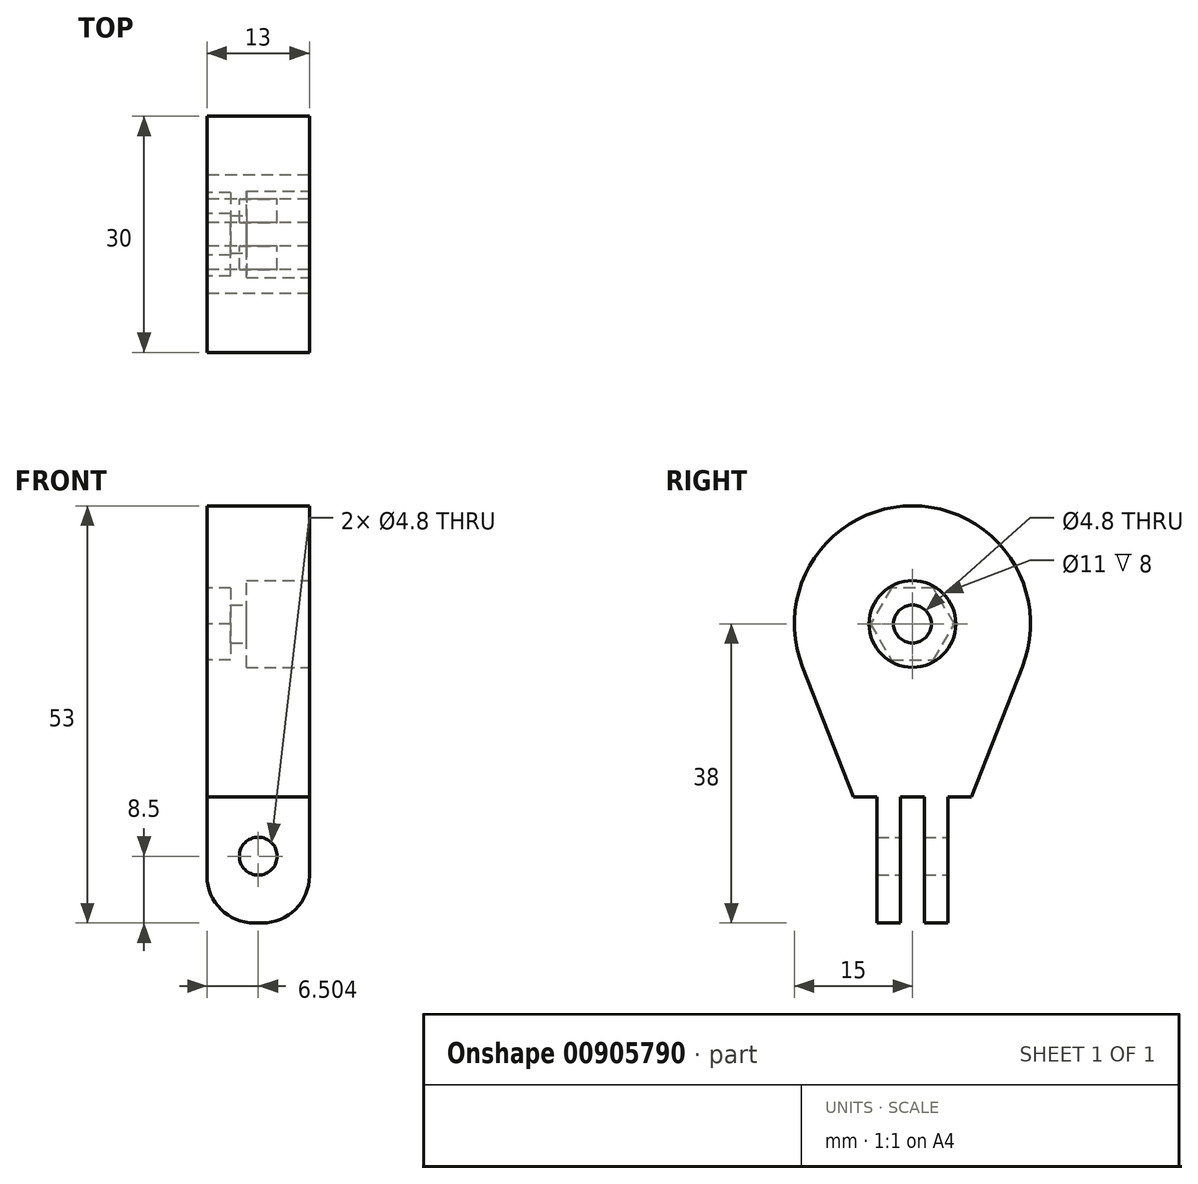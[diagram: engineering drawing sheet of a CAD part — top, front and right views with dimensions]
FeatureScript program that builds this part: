
annotation { "Feature Type Name" : "Feature", "Feature Type Description" : "" }
export const myFeature = defineFeature(function(context is Context, id is Id, definition is map)
    precondition{}
    {
        {
            var Q0;
            Q0=qCreatedBy(makeId("Top.planeOp"),FACE);
            var sketch = newSketch(context, id + "F0", { "sketchPlane" : qUnion([Q0])});
            skLineSegment(sketch, "E0.right", {"start": v(52.22, -25.13) * mm, "end": v(52.22, -14.87) * mm});
            skPoint(sketch, "E0.middle", {"position": v(48.22, 0) * mm});
            skLineSegment(sketch, "E1.bottom", {"start": v(52.22, 30) * mm, "end": v(43.22, 30) * mm});
            skLineSegment(sketch, "E1.top", {"start": v(52.22, -30) * mm, "end": v(43.22, -30) * mm});
            skLineSegment(sketch, "E1.left", {"start": v(52.22, 30) * mm, "end": v(52.22, -30) * mm});
            skLineSegment(sketch, "E1.right", {"start": v(43.22, 30) * mm, "end": v(43.22, -30) * mm});
            skPoint(sketch, "E2.visualSharp", {"position": v(43.22, 30) * mm});
            skLineSegment(sketch, "E2.filletArc", {"start": v(43.22, 30) * mm, "end": v(43.22, 30) * mm});
            skPoint(sketch, "E3.visualSharp", {"position": v(43.22, -30) * mm});
            skLineSegment(sketch, "E3.filletArc", {"start": v(43.22, -30) * mm, "end": v(43.22, -30) * mm});
            skPoint(sketch, "E4.visualSharp", {"position": v(52.22, 30) * mm});
            skLineSegment(sketch, "E4.filletArc", {"start": v(52.22, 30) * mm, "end": v(52.22, 30) * mm});
            skPoint(sketch, "E5.visualSharp", {"position": v(52.22, -30) * mm});
            skLineSegment(sketch, "E5.filletArc", {"start": v(52.22, -30) * mm, "end": v(52.22, -30) * mm});
            skSolve(sketch);
        }
        {
            var Q0;
            Q0=makeQuery(id+"F0.imprint","IMPRINT",FACE,{"disambiguationData":[TD([[makeQuery(id+"F0.imprint","IMPRINT",EDGE,{"derivedFrom":sQuery(id+"F0.wireOp",EDGE,"E1.bottom")}),1.0]])]});
            extrude(context, id + "F1", {"entities" : qUnion([Q0]), "depth" : 30 * mm, "offsetDistance" : 25 * mm, "hasSecondDirection" : true, "secondDirectionOppositeDirection" : true, "secondDirectionDepth" : 22 * mm});
        }
        {
            var Q0;
            Q0=makeQuery(id+"F1.opExtrude","SWEPT_FACE",FACE,{"disambiguationData":[OSD([sQuery(id+"F0.wireOp",EDGE,"E1.left")])]});
            var sketch = newSketch(context, id + "F2", { "sketchPlane" : qUnion([Q0])});
            skCircle(sketch, "E6", {"center": v(0, 0) * mm, "radius": 5.5 * mm});
            skCircle(sketch, "E7", {"center": v(0, 0) * mm, "radius": 2.4 * mm});
            skSolve(sketch);
        }
        {
            var Q0;
            Q0=makeQuery(id+"F2.imprint","IMPRINT",FACE,{"disambiguationData":[TD([[makeQuery(id+"F2.imprint","IMPRINT",EDGE,{"derivedFrom":sQuery(id+"F2.wireOp",EDGE,"E7")}),-1.0]])]});
            var Q1;
            {var subQ0=sQuery(id+"F2.wireOp",EDGE,"E6");var subQ1=sQuery(id+"F0.wireOp",EDGE,"E1.left");var subQ2=makeQuery(id+"Ft0UKXCdEgkPogb_1.opFillet","BLEND_EDGE",EDGE,{"blendedFrom":[makeQuery(id+"F1.opExtrude","CAP_EDGE",EDGE,{"disambiguationData":[OSD([subQ1])],"isStart":false}),makeQuery(id+"F1.opExtrude","SWEPT_FACE",FACE,{"disambiguationData":[OSD([subQ1])]})],"blendedInto":[makeQuery(id+"F1.opExtrude","SWEPT_FACE",FACE,{"disambiguationData":[OSD([subQ1])]})]});var subQ3=makeQuery(id+"F2.imprint","INTERSECT",VERTEX,{"disambiguationData":[OD(0.0)],"derivedFrom":[subQ2,subQ0]});Q1=makeQuery(id+"F2.imprint","IMPRINT",FACE,{"disambiguationData":[TD([[makeQuery(id+"F2.imprint","IMPRINT",EDGE,{"disambiguationData":[TD([[subQ3,-1.0]])],"derivedFrom":subQ0}),1.0]])]});}
            extrude(context, id + "F3", {"entities" : qUnion([Q0, Q1]), "operationType" : NewBodyOperationType.REMOVE, "oppositeDirection" : true, "depth" : 4 * mm, "offsetDistance" : 25 * mm});
        }
        {
            var Q0;
            Q0=makeQuery(id+"F3.boolean.opBoolean","SPLIT",FACE,{"disambiguationData":[TD([makeQuery(id+"F3.opExtrude","SWEPT_FACE",FACE,{"disambiguationData":[OSD([sQuery(id+"F2.wireOp",EDGE,"E7")])]})])],"derivedFrom":makeQuery(id+"F1.opExtrude","SWEPT_FACE",FACE,{"disambiguationData":[OSD([sQuery(id+"F0.wireOp",EDGE,"E1.left")])]})});
            extrude(context, id + "F4", {"entities" : qUnion([Q0]), "operationType" : NewBodyOperationType.REMOVE, "oppositeDirection" : true, "depth" : 10.6 * mm, "offsetDistance" : 25 * mm});
        }
        {
            var Q0;
            Q0=makeQuery(id+"F1.opExtrude","SWEPT_FACE",FACE,{"disambiguationData":[OSD([sQuery(id+"F0.wireOp",EDGE,"E1.right")])]});
            var sketch = newSketch(context, id + "F5", { "sketchPlane" : qUnion([Q0])});
            skCircle(sketch, "E8.cCircle", {"center": v(0, 0) * mm, "radius": 5.31 * mm, "construction": true});
            skLineSegment(sketch, "E8.0", {"start": v(5.31, 0) * mm, "end": v(2.66, -4.6) * mm});
            skLineSegment(sketch, "E8.1", {"start": v(2.66, -4.6) * mm, "end": v(-2.66, -4.6) * mm});
            skLineSegment(sketch, "E8.2", {"start": v(-2.66, -4.6) * mm, "end": v(-5.31, 0) * mm});
            skLineSegment(sketch, "E8.3", {"start": v(-5.31, 0) * mm, "end": v(-2.66, 4.6) * mm});
            skLineSegment(sketch, "E8.4", {"start": v(-2.66, 4.6) * mm, "end": v(2.66, 4.6) * mm});
            skLineSegment(sketch, "E8.5", {"start": v(2.66, 4.6) * mm, "end": v(5.31, 0) * mm});
            skSolve(sketch);
        }
        {
            var Q0;
            {var subQ8=sQuery(id+"F5.wireOp",EDGE,"E8.0");Q0=makeQuery(id+"F5.imprint","IMPRINT",FACE,{"disambiguationData":[TD([[makeQuery(id+"F5.imprint","IMPRINT",EDGE,{"derivedFrom":subQ8}),-1.0]])]});}
            var Q1;
            {var subQ0=sQuery(id+"F5.wireOp",EDGE,"E8.4");Q1=makeQuery(id+"F5.imprint","IMPRINT",FACE,{"disambiguationData":[TD([[makeQuery(id+"F5.imprint","IMPRINT",EDGE,{"derivedFrom":subQ0}),-1.0]])]});}
            extrude(context, id + "F6", {"entities" : qUnion([Q0, Q1]), "operationType" : NewBodyOperationType.REMOVE, "oppositeDirection" : true, "depth" : 3 * mm, "offsetDistance" : 25 * mm});
        }
        {
            var Q0;
            Q0=makeQuery(id+"F1.opExtrude","SWEPT_FACE",FACE,{"disambiguationData":[OSD([sQuery(id+"F0.wireOp",EDGE,"E1.right")])]});
            var sketch = newSketch(context, id + "F7", { "sketchPlane" : qUnion([Q0])});
            skArc(sketch, "E9", {"start": v(13.97, -5.47) * mm, "mid": v(0, 15) * mm, "end": v(-13.97, -5.47) * mm});
            skLineSegment(sketch, "E10", {"start": v(0, -22) * mm, "end": v(-7.5, -22) * mm});
            skLineSegment(sketch, "E11", {"start": v(-7.5, -22) * mm, "end": v(-13.97, -5.47) * mm});
            skLineSegment(sketch, "E12.MirrorCS", {"start": v(7.5, -22) * mm, "end": v(13.97, -5.47) * mm});
            skLineSegment(sketch, "E13.MirrorCS", {"start": v(0, -22) * mm, "end": v(7.5, -22) * mm});
            skSolve(sketch);
        }
        {
            var Q0;
            Q0=makeQuery(id+"F7.imprint","IMPRINT",FACE,{"disambiguationData":[TD([[makeQuery(id+"F7.imprint","IMPRINT",EDGE,{"derivedFrom":sQuery(id+"F7.wireOp",EDGE,"E9")}),-1.0]])]});
            extrude(context, id + "F8", {"entities" : qUnion([Q0]), "operationType" : NewBodyOperationType.REMOVE, "oppositeDirection" : true, "depth" : 25 * mm, "offsetDistance" : 25 * mm});
        }
        {
            var Q0;
            {var subQ2=sQuery(id+"F0.wireOp",EDGE,"E1.left");var subQ3=sQuery(id+"F0.wireOp",EDGE,"E1.bottom");Q0=makeQuery(id+"F3.boolean.opBoolean","SPLIT",FACE,{"disambiguationData":[TD([makeQuery(id+"F1.opExtrude","SWEPT_FACE",FACE,{"disambiguationData":[OSD([subQ3])]})])],"derivedFrom":makeQuery(id+"F1.opExtrude","SWEPT_FACE",FACE,{"disambiguationData":[OSD([subQ2])]})});}
            extrude(context, id + "F9", {"entities" : qUnion([Q0]), "operationType" : NewBodyOperationType.ADD, "depth" : 4 * mm, "offsetDistance" : 25 * mm});
        }
        {
            var Q0;
            {var subQ0=sQuery(id+"F0.wireOp",EDGE,"E1.left");Q0=makeQuery(id+"F9.boolean.opBoolean","MERGE",FACE,{"derivedFrom":[makeQuery(id+"F1.opExtrude","CAP_FACE",FACE,{"disambiguationData":[OSD([sQuery(id+"F0.wireOp",EDGE,"E1.bottom"),sQuery(id+"F0.wireOp",EDGE,"E1.top"),subQ0,sQuery(id+"F0.wireOp",EDGE,"E1.right")])],"isStart":true}),makeQuery(id+"F9.opExtrude","SWEPT_FACE",FACE,{"disambiguationData":[OSD([subQ0])]})]});}
            var sketch = newSketch(context, id + "F10", { "sketchPlane" : qUnion([Q0])});
            skLineSegment(sketch, "E14", {"start": v(56.22, 0) * mm, "end": v(56.22, -1.5) * mm});
            skLineSegment(sketch, "E15.bottom", {"start": v(56.22, -1.5) * mm, "end": v(43.22, -1.5) * mm});
            skLineSegment(sketch, "E15.top", {"start": v(56.22, -4.5) * mm, "end": v(43.22, -4.5) * mm});
            skLineSegment(sketch, "E15.left", {"start": v(56.22, -1.5) * mm, "end": v(56.22, -4.5) * mm});
            skLineSegment(sketch, "E15.right", {"start": v(43.22, -1.5) * mm, "end": v(43.22, -4.5) * mm});
            skLineSegment(sketch, "E16.MirrorCS", {"start": v(56.22, 1.5) * mm, "end": v(43.22, 1.5) * mm});
            skLineSegment(sketch, "E17.MirrorCS", {"start": v(56.22, 4.5) * mm, "end": v(43.22, 4.5) * mm});
            skLineSegment(sketch, "E18.MirrorCS", {"start": v(43.22, 1.5) * mm, "end": v(43.22, 4.5) * mm});
            skLineSegment(sketch, "E19.MirrorCS", {"start": v(56.22, 1.5) * mm, "end": v(56.22, 4.5) * mm});
            skSolve(sketch);
        }
        {
            var Q0;
            Q0=makeQuery(id+"F10.imprint","IMPRINT",FACE,{"disambiguationData":[TD([[makeQuery(id+"F10.imprint","IMPRINT",EDGE,{"derivedFrom":sQuery(id+"F10.wireOp",EDGE,"E15.bottom")}),1.0]])]});
            var Q1;
            Q1=makeQuery(id+"F10.imprint","IMPRINT",FACE,{"disambiguationData":[TD([[makeQuery(id+"F10.imprint","IMPRINT",EDGE,{"derivedFrom":sQuery(id+"F10.wireOp",EDGE,"E16.MirrorCS")}),-1.0]])]});
            extrude(context, id + "F11", {"entities" : qUnion([Q0, Q1]), "operationType" : NewBodyOperationType.ADD, "depth" : 16 * mm, "offsetDistance" : 25 * mm});
        }
        {
            var Q0;
            Q0=makeQuery(id+"F11.opExtrude","CAP_EDGE",EDGE,{"disambiguationData":[OSD([sQuery(id+"F10.wireOp",EDGE,"E18.MirrorCS")])],"isStart":false});
            var Q1;
            Q1=makeQuery(id+"F11.opExtrude","CAP_EDGE",EDGE,{"disambiguationData":[OSD([sQuery(id+"F10.wireOp",EDGE,"E15.right")])],"isStart":false});
            var Q2;
            Q2=makeQuery(id+"F11.opExtrude","CAP_EDGE",EDGE,{"disambiguationData":[OSD([sQuery(id+"F10.wireOp",EDGE,"E15.left")])],"isStart":false});
            var Q3;
            Q3=makeQuery(id+"F11.opExtrude","CAP_EDGE",EDGE,{"disambiguationData":[OSD([sQuery(id+"F10.wireOp",EDGE,"E19.MirrorCS")])],"isStart":false});
            fillet(context, id + "F12", {"entities" : qUnion([Q0, Q1, Q2, Q3]), "radius" : 6 * mm, "tangentPropagation" : true, "allowEdgeOverflow" : false});
        }
        {
            var Q0;
            Q0=makeQuery(id+"F11.opExtrude","SWEPT_FACE",FACE,{"disambiguationData":[OSD([sQuery(id+"F10.wireOp",EDGE,"E15.top")])]});
            var sketch = newSketch(context, id + "F13", { "sketchPlane" : qUnion([Q0])});
            skLineSegment(sketch, "E20", {"start": v(-49.72, -22) * mm, "end": v(-49.72, -29.5) * mm, "construction": true});
            skCircle(sketch, "E21", {"center": v(-49.72, -29.5) * mm, "radius": 2.4 * mm});
            skSolve(sketch);
        }
        {
            var Q0;
            Q0=makeQuery(id+"F13.imprint","IMPRINT",FACE,{"disambiguationData":[TD([[makeQuery(id+"F13.imprint","IMPRINT",EDGE,{"derivedFrom":sQuery(id+"F13.wireOp",EDGE,"E21")}),1.0]])]});
            extrude(context, id + "F14", {"entities" : qUnion([Q0]), "operationType" : NewBodyOperationType.REMOVE, "oppositeDirection" : true, "depth" : 25 * mm, "offsetDistance" : 25 * mm});
        }
    });
